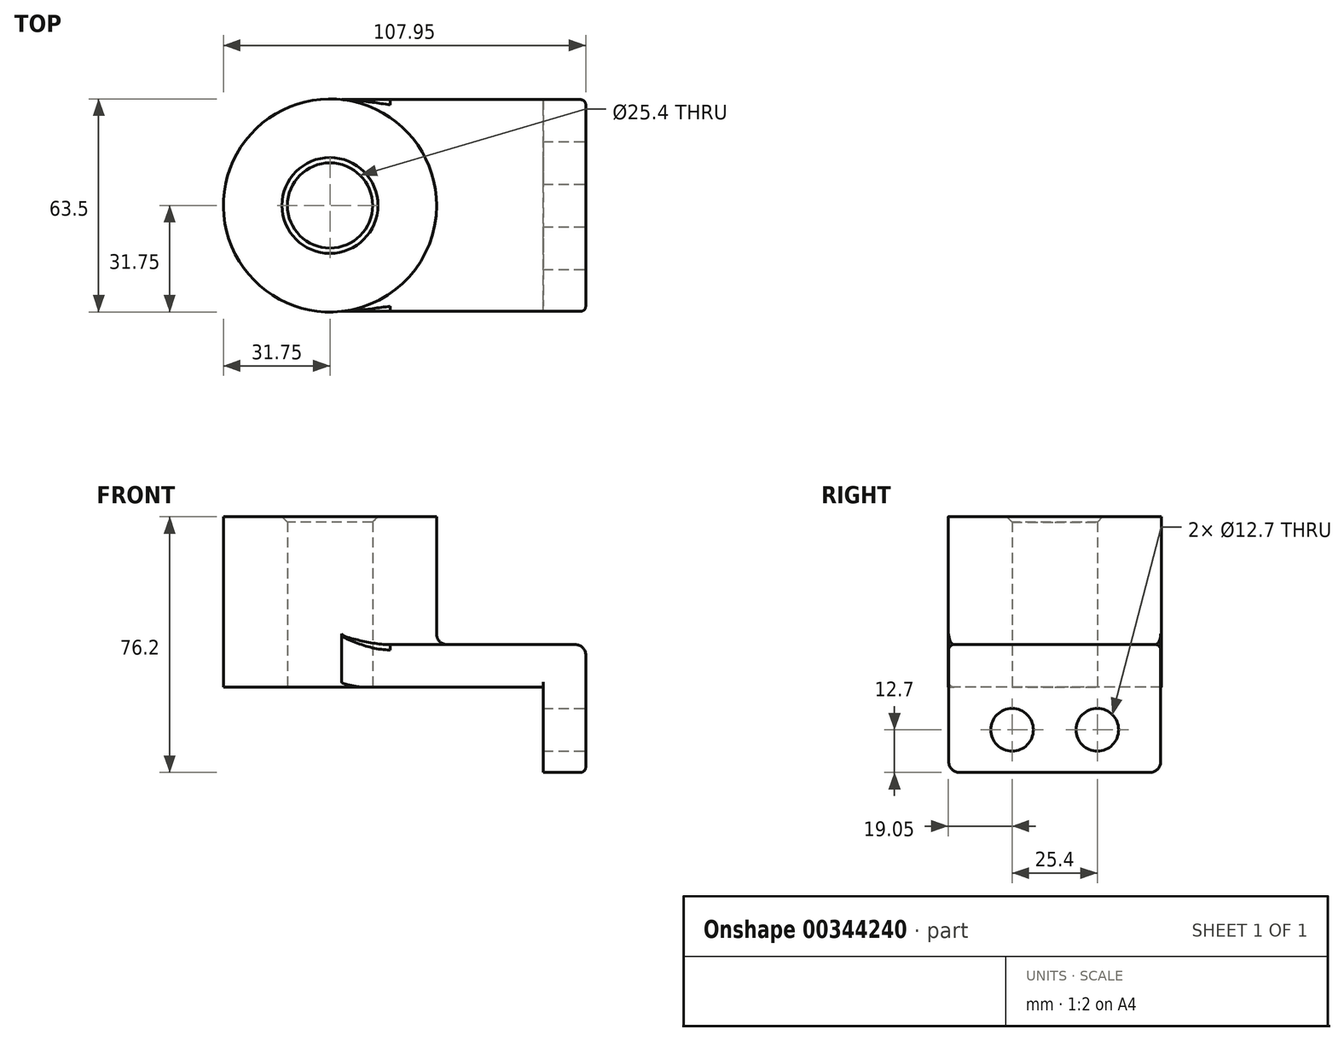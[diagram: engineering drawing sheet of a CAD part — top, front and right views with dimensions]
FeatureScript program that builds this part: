
annotation { "Feature Type Name" : "Feature", "Feature Type Description" : "" }
export const myFeature = defineFeature(function(context is Context, id is Id, definition is map)
    precondition{}
    {
        {
            var Q0;
            Q0=qCreatedBy(makeId("Top.planeOp"),FACE);
            var sketch = newSketch(context, id + "F0", { "sketchPlane" : qUnion([Q0])});
            skLineSegment(sketch, "E0.bottom", {"start": v(38.1, 31.57) * mm, "end": v(-38.1, 31.57) * mm});
            skLineSegment(sketch, "E0.top", {"start": v(38.1, -31.57) * mm, "end": v(-38.1, -31.57) * mm});
            skLineSegment(sketch, "E0.left", {"start": v(38.1, 31.57) * mm, "end": v(38.1, -31.57) * mm});
            skLineSegment(sketch, "E0.right", {"start": v(-38.1, 31.57) * mm, "end": v(-38.1, -31.57) * mm});
            skPoint(sketch, "E0.middle", {"position": v(0, 0) * mm});
            skCircle(sketch, "E1", {"center": v(-38.1, 0) * mm, "radius": 31.75 * mm});
            skCircle(sketch, "E2", {"center": v(-38.1, 0) * mm, "radius": 12.7 * mm});
            skSolve(sketch);
        }
        {
            var Q0;
            {var subQ0=sQuery(id+"F0.wireOp",EDGE,"E0.left");Q0=makeQuery(id+"F0.imprint","IMPRINT",FACE,{"disambiguationData":[TD([[makeQuery(id+"F0.imprint","IMPRINT",EDGE,{"derivedFrom":subQ0}),-1.0]])]});}
            var Q1;
            {var subQ0=sQuery(id+"F0.wireOp",EDGE,"E0.right");var subQ5=sQuery(id+"F0.wireOp",EDGE,"E0.bottom");var subQ6=makeQuery(id+"F0.imprint","INTERSECT",VERTEX,{"derivedFrom":[subQ5,subQ0]});Q1=makeQuery(id+"F0.imprint","IMPRINT",FACE,{"disambiguationData":[TD([[makeQuery(id+"F0.imprint","IMPRINT",EDGE,{"disambiguationData":[TD([[subQ6,1.0]])],"derivedFrom":subQ5}),-1.0]])]});}
            var Q2;
            {var subQ0=sQuery(id+"F0.wireOp",EDGE,"E0.right");var subQ5=sQuery(id+"F0.wireOp",EDGE,"E0.bottom");var subQ6=makeQuery(id+"F0.imprint","INTERSECT",VERTEX,{"derivedFrom":[subQ5,subQ0]});Q2=makeQuery(id+"F0.imprint","IMPRINT",FACE,{"disambiguationData":[TD([[makeQuery(id+"F0.imprint","IMPRINT",EDGE,{"disambiguationData":[TD([[subQ6,1.0]])],"derivedFrom":subQ5}),1.0]])]});}
            extrude(context, id + "F1", {"entities" : qUnion([Q0, Q1, Q2]), "depth" : 12.7 * mm});
        }
        {
            var Q0;
            {var subQ0=sQuery(id+"F0.wireOp",EDGE,"E0.right");var subQ5=sQuery(id+"F0.wireOp",EDGE,"E0.bottom");var subQ6=makeQuery(id+"F0.imprint","INTERSECT",VERTEX,{"derivedFrom":[subQ5,subQ0]});Q0=makeQuery(id+"F0.imprint","IMPRINT",FACE,{"disambiguationData":[TD([[makeQuery(id+"F0.imprint","IMPRINT",EDGE,{"disambiguationData":[TD([[subQ6,1.0]])],"derivedFrom":subQ5}),-1.0]])]});}
            var Q1;
            {var subQ0=sQuery(id+"F0.wireOp",EDGE,"E0.right");var subQ5=sQuery(id+"F0.wireOp",EDGE,"E0.bottom");var subQ6=makeQuery(id+"F0.imprint","INTERSECT",VERTEX,{"derivedFrom":[subQ5,subQ0]});Q1=makeQuery(id+"F0.imprint","IMPRINT",FACE,{"disambiguationData":[TD([[makeQuery(id+"F0.imprint","IMPRINT",EDGE,{"disambiguationData":[TD([[subQ6,1.0]])],"derivedFrom":subQ5}),1.0]])]});}
            extrude(context, id + "F2", {"entities" : qUnion([Q0, Q1]), "operationType" : NewBodyOperationType.ADD, "depth" : 50.8 * mm});
        }
        {
            var Q0;
            Q0=makeQuery(id+"F1.opExtrude","SWEPT_FACE",FACE,{"disambiguationData":[OSD([sQuery(id+"F0.wireOp",EDGE,"E0.left")])]});
            var sketch = newSketch(context, id + "F3", { "sketchPlane" : qUnion([Q0])});
            skLineSegment(sketch, "E3.bottom", {"start": v(-31.57, 12.7) * mm, "end": v(31.57, 12.7) * mm});
            skLineSegment(sketch, "E3.top", {"start": v(-31.57, -25.4) * mm, "end": v(31.57, -25.4) * mm});
            skLineSegment(sketch, "E3.left", {"start": v(-31.57, 12.7) * mm, "end": v(-31.57, -25.4) * mm});
            skLineSegment(sketch, "E3.right", {"start": v(31.57, 12.7) * mm, "end": v(31.57, -25.4) * mm});
            skLineSegment(sketch, "E4", {"start": v(0, 0) * mm, "end": v(0, -25.4) * mm});
            skCircle(sketch, "E5", {"center": v(-12.7, -12.7) * mm, "radius": 6.35 * mm});
            skCircle(sketch, "E6.MirrorC", {"center": v(12.7, -12.7) * mm, "radius": 6.35 * mm});
            skSolve(sketch);
        }
        {
            var Q0;
            {var subQ0=sQuery(id+"F3.wireOp",EDGE,"E4");Q0=makeQuery(id+"F3.imprint","IMPRINT",FACE,{"disambiguationData":[TD([[makeQuery(id+"F3.imprint","IMPRINT",EDGE,{"derivedFrom":subQ0}),-1.0]])]});}
            var Q1;
            {var subQ5=sQuery(id+"F3.wireOp",EDGE,"E4");Q1=makeQuery(id+"F3.imprint","IMPRINT",FACE,{"disambiguationData":[TD([[makeQuery(id+"F3.imprint","IMPRINT",EDGE,{"derivedFrom":subQ5}),1.0]])]});}
            extrude(context, id + "F4", {"entities" : qUnion([Q0, Q1]), "operationType" : NewBodyOperationType.ADD, "oppositeDirection" : true, "depth" : 12.7 * mm});
        }
        {
            var Q0;
            {var subQ0=sQuery(id+"F0.wireOp",EDGE,"E1");Q0=makeQuery(id+"F2.boolean.opBoolean","INTERSECT",EDGE,{"derivedFrom":[makeQuery(id+"F1.opExtrude","CAP_FACE",FACE,{"disambiguationData":[OSD([sQuery(id+"F0.wireOp",EDGE,"E0.bottom"),sQuery(id+"F0.wireOp",EDGE,"E0.top"),sQuery(id+"F0.wireOp",EDGE,"E0.left"),subQ0,sQuery(id+"F0.wireOp",EDGE,"E2")])],"isStart":false}),makeQuery(id+"F2.opExtrude","SWEPT_FACE",FACE,{"disambiguationData":[OSD([subQ0])]})]});}
            var Q1;
            Q1=makeQuery(id+"F1.opExtrude","CAP_EDGE",EDGE,{"disambiguationData":[OSD([sQuery(id+"F0.wireOp",EDGE,"E0.left")])],"isStart":false});
            var Q2;
            Q2=makeQuery(id+"F4.opExtrude","SWEPT_EDGE",EDGE,{"disambiguationData":[OSD([sQuery(id+"F3.wireOp",EDGE,"E3.top"),sQuery(id+"F3.wireOp",EDGE,"E3.left")])]});
            var Q3;
            Q3=makeQuery(id+"F4.opExtrude","SWEPT_EDGE",EDGE,{"disambiguationData":[OSD([sQuery(id+"F3.wireOp",EDGE,"E3.top"),sQuery(id+"F3.wireOp",EDGE,"E3.right")])]});
            fillet(context, id + "F5", {"entities" : qUnion([Q0, Q1, Q2, Q3]), "radius" : 3.17 * mm, "tangentPropagation" : true, "allowEdgeOverflow" : false});
        }
        {
            var Q0;
            Q0=makeQuery(id+"F1.opExtrude","CAP_EDGE",EDGE,{"disambiguationData":[OSD([sQuery(id+"F0.wireOp",EDGE,"E0.top")])],"isStart":false});
            var Q1;
            Q1=makeQuery(id+"F1.opExtrude","CAP_EDGE",EDGE,{"disambiguationData":[OSD([sQuery(id+"F0.wireOp",EDGE,"E0.top")])],"isStart":true});
            var Q2;
            Q2=makeQuery(id+"F4.opExtrude","CAP_EDGE",EDGE,{"disambiguationData":[OSD([sQuery(id+"F0.wireOp",EDGE,"E0.left")])],"isStart":false});
            fillet(context, id + "F6", {"entities" : qUnion([Q0, Q1, Q2]), "radius" : 1.59 * mm, "tangentPropagation" : true, "allowEdgeOverflow" : false});
        }
        {
            var Q0;
            Q0=makeQuery(id+"F2.opExtrude","CAP_EDGE",EDGE,{"disambiguationData":[OSD([sQuery(id+"F0.wireOp",EDGE,"E2")])],"isStart":false});
            chamfer(context, id + "F7", {"entities" : qUnion([Q0]), "width" : 1.59 * mm, "tangentPropagation" : true});
        }
    });
